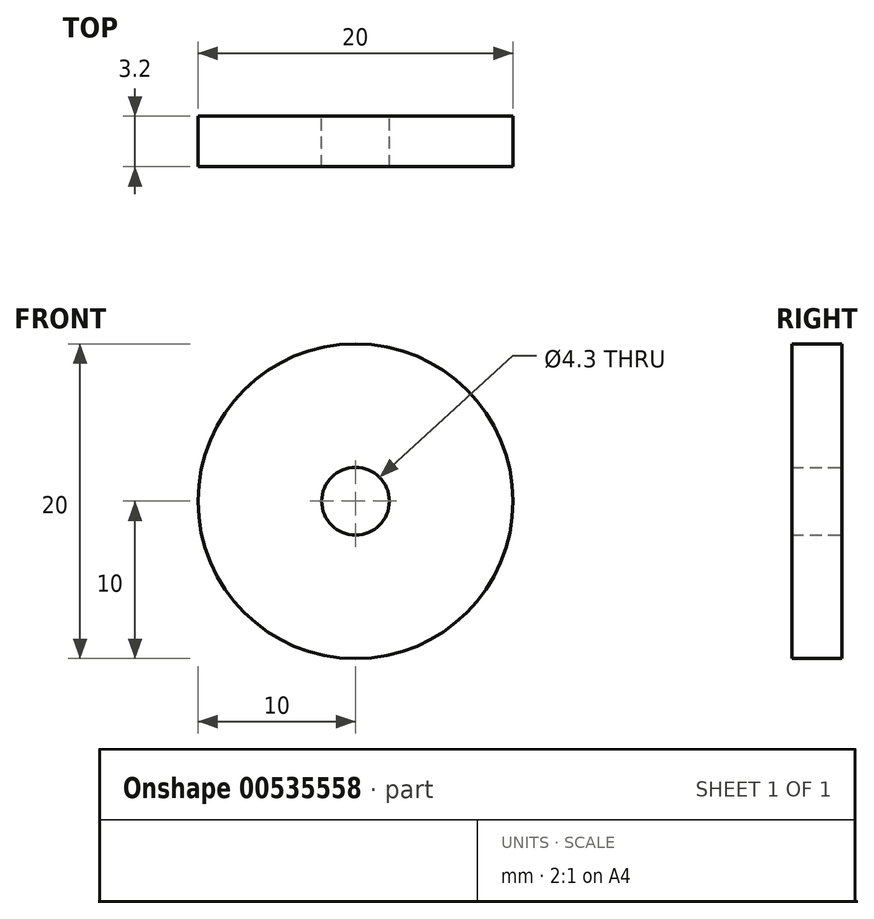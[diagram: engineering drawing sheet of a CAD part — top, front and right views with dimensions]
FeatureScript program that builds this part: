
annotation { "Feature Type Name" : "Feature", "Feature Type Description" : "" }
export const myFeature = defineFeature(function(context is Context, id is Id, definition is map)
    precondition{}
    {
        {
            var Q0;
            Q0=qCreatedBy(makeId("Front.planeOp"),FACE);
            var sketch = newSketch(context, id + "F0", { "sketchPlane" : qUnion([Q0])});
            skCircle(sketch, "E0", {"center": v(0, 0) * mm, "radius": 10 * mm});
            skCircle(sketch, "E1", {"center": v(0, 0) * mm, "radius": 2.15 * mm});
            skSolve(sketch);
        }
        {
            var Q0;
            Q0 = qSketchRegion(id + "F0", true);
            extrude(context, id + "F1", {"entities" : qUnion([Q0]), "depth" : 3.2 * mm, "offsetDistance" : 25 * mm});
        }
    });
